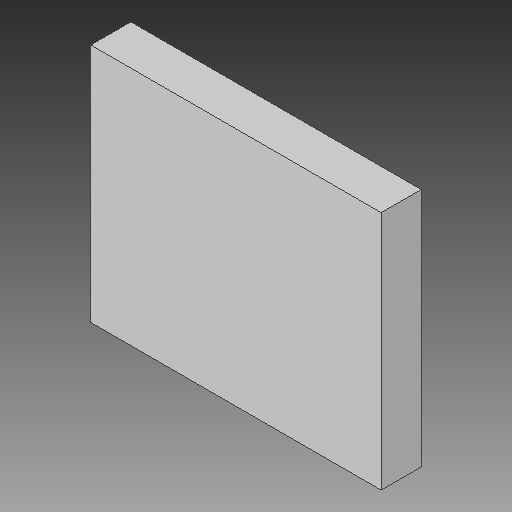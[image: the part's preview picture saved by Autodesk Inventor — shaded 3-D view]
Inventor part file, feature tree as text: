
AUTODESK INVENTOR PART (.ipt)
format: ipt  version: 2018 (Build 220112000, 112)  size: 84,480 bytes
history: native  units: mm
features: extrude x1, sketch x1
ambient origin geometry x8: Origin, YZ Plane, XZ Plane, XY Plane, X Axis, Y Axis, Z Axis, Center Point
bodies: Solid1 (feature_tree)
feature tree (2):
  extrude  "Extrusion1"  Depth=48.0mm
  sketch  "Sketch1"  dims[d0=58.0mm d1=48.0mm d2=8.0mm d3=0.0mm]
